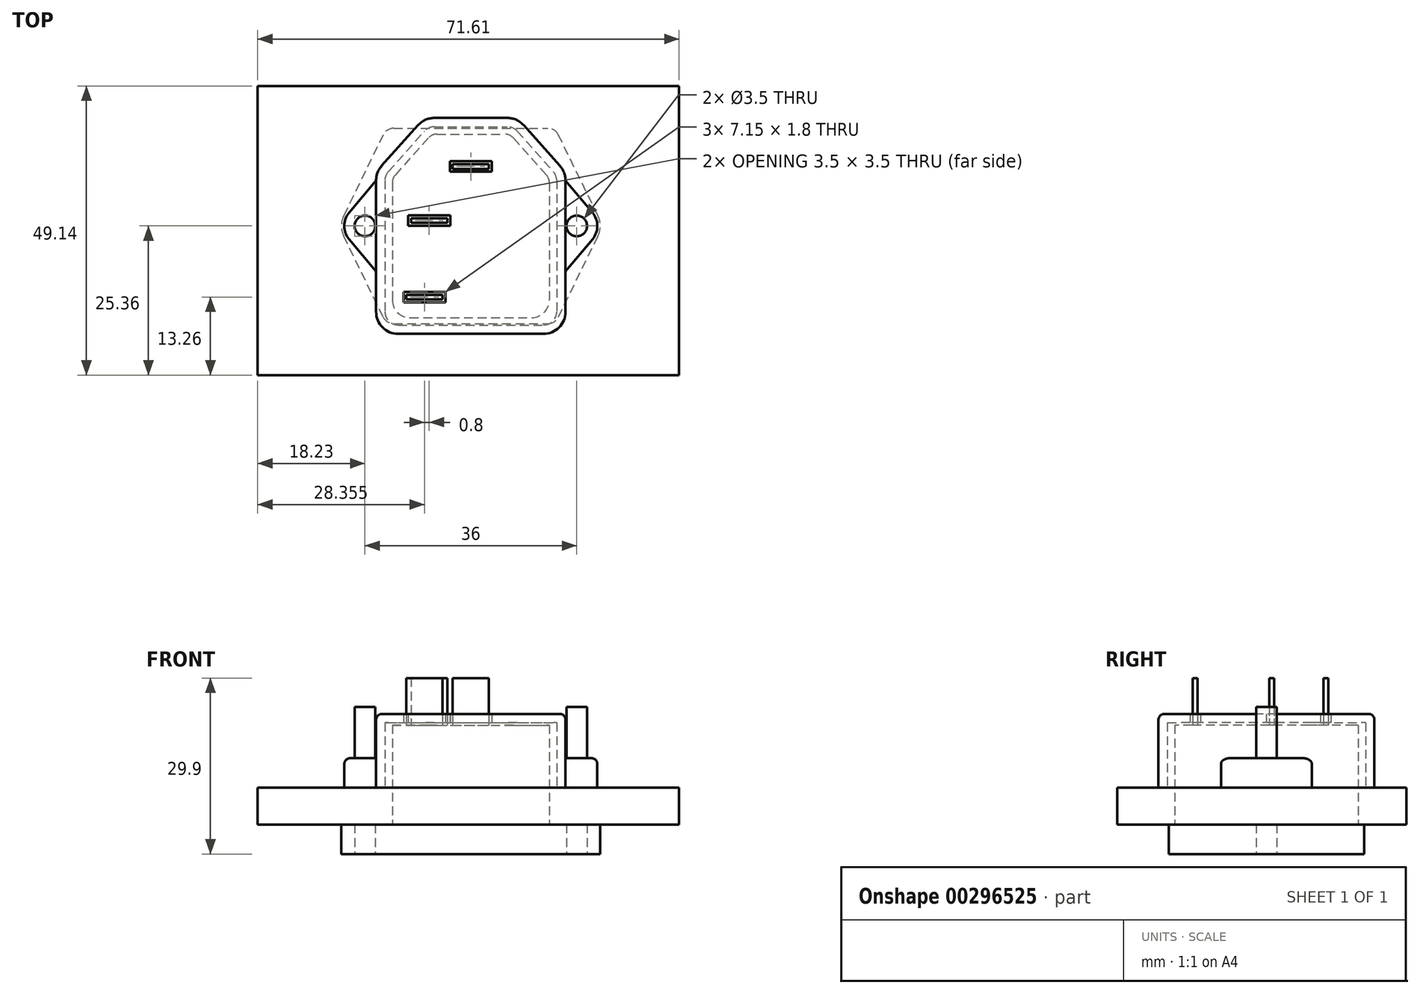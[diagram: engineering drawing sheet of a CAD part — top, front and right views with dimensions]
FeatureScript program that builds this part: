
annotation { "Feature Type Name" : "Feature", "Feature Type Description" : "" }
export const myFeature = defineFeature(function(context is Context, id is Id, definition is map)
    precondition{}
    {
        {
            var Q0;
            Q0=qCreatedBy(makeId("Top.planeOp"),FACE);
            var sketch = newSketch(context, id + "F0", { "sketchPlane" : qUnion([Q0])});
            skLineSegment(sketch, "E0.bottom", {"start": v(-5.75, 13.24) * mm, "end": v(5.75, 13.24) * mm});
            skLineSegment(sketch, "E0.top", {"start": v(-10.35, -17.96) * mm, "end": v(10.35, -17.96) * mm});
            skLineSegment(sketch, "E0.left", {"start": v(-13.35, 4.98) * mm, "end": v(-13.35, -14.96) * mm});
            skLineSegment(sketch, "E0.right", {"start": v(13.35, 4.98) * mm, "end": v(13.35, -14.96) * mm});
            skLineSegment(sketch, "E1", {"start": v(-7.25, 12.57) * mm, "end": v(-12.84, 6.3) * mm});
            skLineSegment(sketch, "E2", {"start": v(7.25, 12.57) * mm, "end": v(12.84, 6.3) * mm});
            skPoint(sketch, "E3.orphan", {"position": v(-13.35, 13.24) * mm});
            skPoint(sketch, "E4.orphan", {"position": v(13.35, 13.24) * mm});
            skPoint(sketch, "E5.visualSharp", {"position": v(-6.65, 13.24) * mm});
            skArc(sketch, "E5.filletArc", {"start": v(-5.75, 13.24) * mm, "mid": v(-6.57, 13.07) * mm, "end": v(-7.25, 12.57) * mm});
            skPoint(sketch, "E6.visualSharp", {"position": v(6.65, 13.24) * mm});
            skArc(sketch, "E6.filletArc", {"start": v(7.25, 12.57) * mm, "mid": v(6.57, 13.07) * mm, "end": v(5.75, 13.24) * mm});
            skPoint(sketch, "E7.visualSharp", {"position": v(13.35, 5.74) * mm});
            skArc(sketch, "E7.filletArc", {"start": v(13.35, 4.98) * mm, "mid": v(13.22, 5.69) * mm, "end": v(12.84, 6.3) * mm});
            skPoint(sketch, "E8.visualSharp", {"position": v(-13.35, 5.74) * mm});
            skArc(sketch, "E8.filletArc", {"start": v(-12.84, 6.3) * mm, "mid": v(-13.22, 5.69) * mm, "end": v(-13.35, 4.98) * mm});
            skPoint(sketch, "E9.visualSharp", {"position": v(-13.35, -17.96) * mm});
            skArc(sketch, "E9.filletArc", {"start": v(-13.35, -14.96) * mm, "mid": v(-12.47, -17.08) * mm, "end": v(-10.35, -17.96) * mm});
            skPoint(sketch, "E10.visualSharp", {"position": v(13.35, -17.96) * mm});
            skArc(sketch, "E10.filletArc", {"start": v(10.35, -17.96) * mm, "mid": v(12.47, -17.08) * mm, "end": v(13.35, -14.96) * mm});
            skSolve(sketch);
        }
        {
            var Q0;
            Q0=makeQuery(id+"F0.imprint","IMPRINT",FACE,{"disambiguationData":[TD([[makeQuery(id+"F0.imprint","IMPRINT",EDGE,{"derivedFrom":sQuery(id+"F0.wireOp",EDGE,"E0.bottom")}),-1.0]])]});
            extrude(context, id + "F1", {"entities" : qUnion([Q0]), "depth" : 16.9 * mm});
        }
        {
            var Q0;
            Q0=makeQuery(id+"F1.opExtrude","CAP_FACE",FACE,{"disambiguationData":[OSD([sQuery(id+"F0.wireOp",EDGE,"E0.bottom"),sQuery(id+"F0.wireOp",EDGE,"E0.top"),sQuery(id+"F0.wireOp",EDGE,"E0.left"),sQuery(id+"F0.wireOp",EDGE,"E0.right"),sQuery(id+"F0.wireOp",EDGE,"E1"),sQuery(id+"F0.wireOp",EDGE,"E2"),sQuery(id+"F0.wireOp",EDGE,"E5.filletArc"),sQuery(id+"F0.wireOp",EDGE,"E6.filletArc"),sQuery(id+"F0.wireOp",EDGE,"E7.filletArc"),sQuery(id+"F0.wireOp",EDGE,"E8.filletArc"),sQuery(id+"F0.wireOp",EDGE,"E9.filletArc"),sQuery(id+"F0.wireOp",EDGE,"E10.filletArc")])],"isStart":false});
            var sketch = newSketch(context, id + "F2", { "sketchPlane" : qUnion([Q0])});
            skLineSegment(sketch, "E11.bottom", {"start": v(-3.08, 8.14) * mm, "end": v(3.08, 8.14) * mm});
            skLineSegment(sketch, "E11.top", {"start": v(-3.08, 7.34) * mm, "end": v(3.07, 7.34) * mm});
            skLineSegment(sketch, "E11.left", {"start": v(-3.08, 8.14) * mm, "end": v(-3.08, 7.34) * mm});
            skLineSegment(sketch, "E11.right", {"start": v(3.08, 8.14) * mm, "end": v(3.08, 7.34) * mm});
            skLineSegment(sketch, "E12.bottom", {"start": v(-10.15, -1.06) * mm, "end": v(-4, -1.06) * mm});
            skLineSegment(sketch, "E12.top", {"start": v(-10.15, -1.86) * mm, "end": v(-4, -1.86) * mm});
            skLineSegment(sketch, "E12.left", {"start": v(-10.15, -1.06) * mm, "end": v(-10.15, -1.86) * mm});
            skLineSegment(sketch, "E12.right", {"start": v(-4, -1.06) * mm, "end": v(-4, -1.86) * mm});
            skLineSegment(sketch, "E13.bottom", {"start": v(-10.95, -14.06) * mm, "end": v(-4.8, -14.06) * mm});
            skLineSegment(sketch, "E13.top", {"start": v(-10.95, -14.86) * mm, "end": v(-4.8, -14.86) * mm});
            skLineSegment(sketch, "E13.left", {"start": v(-10.95, -14.06) * mm, "end": v(-10.95, -14.86) * mm});
            skLineSegment(sketch, "E13.right", {"start": v(-4.8, -14.06) * mm, "end": v(-4.8, -14.86) * mm});
            skSolve(sketch);
        }
        {
            var Q0;
            Q0 = qSketchRegion(id + "F2", true);
            extrude(context, id + "F3", {"entities" : qUnion([Q0]), "operationType" : NewBodyOperationType.ADD, "depth" : 8 * mm});
        }
        {
            var Q0;
            Q0=makeQuery(id+"F1.opExtrude","CAP_FACE",FACE,{"disambiguationData":[OSD([sQuery(id+"F0.wireOp",EDGE,"E0.bottom"),sQuery(id+"F0.wireOp",EDGE,"E0.top"),sQuery(id+"F0.wireOp",EDGE,"E0.left"),sQuery(id+"F0.wireOp",EDGE,"E0.right"),sQuery(id+"F0.wireOp",EDGE,"E1"),sQuery(id+"F0.wireOp",EDGE,"E2"),sQuery(id+"F0.wireOp",EDGE,"E5.filletArc"),sQuery(id+"F0.wireOp",EDGE,"E6.filletArc"),sQuery(id+"F0.wireOp",EDGE,"E7.filletArc"),sQuery(id+"F0.wireOp",EDGE,"E8.filletArc"),sQuery(id+"F0.wireOp",EDGE,"E9.filletArc"),sQuery(id+"F0.wireOp",EDGE,"E10.filletArc")])],"isStart":true});
            var sketch = newSketch(context, id + "F4", { "sketchPlane" : qUnion([Q0])});
            skLineSegment(sketch, "E14.bottom", {"start": v(-13.1, 18.96) * mm, "end": v(13.1, 18.96) * mm});
            skLineSegment(sketch, "E14.top", {"start": v(-13.1, -14.24) * mm, "end": v(13.1, -14.24) * mm});
            skLineSegment(sketch, "E14.left", {"start": v(-14.35, 18.96) * mm, "end": v(-14.35, 18.52) * mm});
            skLineSegment(sketch, "E14.right", {"start": v(14.35, 18.96) * mm, "end": v(14.35, 18.52) * mm});
            skLineSegment(sketch, "E15", {"start": v(-20.93, 2.36) * mm, "end": v(38.8, 2.36) * mm, "construction": true});
            skCircle(sketch, "E16", {"center": v(18, 2.36) * mm, "radius": 1.75 * mm});
            skCircle(sketch, "E17", {"center": v(-18, 2.36) * mm, "radius": 1.75 * mm});
            skArc(sketch, "E18", {"start": v(-21.6, 4.11) * mm, "mid": v(-22, 2.36) * mm, "end": v(-21.6, 0.6) * mm});
            skArc(sketch, "E19", {"start": v(21.6, 0.6) * mm, "mid": v(22, 2.36) * mm, "end": v(21.6, 4.11) * mm});
            skLineSegment(sketch, "E20", {"start": v(-14.9, 17.84) * mm, "end": v(-21.6, 4.11) * mm});
            skLineSegment(sketch, "E21", {"start": v(-14.9, -13.12) * mm, "end": v(-21.6, 0.6) * mm});
            skLineSegment(sketch, "E22", {"start": v(14.9, 17.84) * mm, "end": v(21.6, 4.11) * mm});
            skLineSegment(sketch, "E23", {"start": v(21.6, 0.6) * mm, "end": v(14.9, -13.12) * mm});
            skPoint(sketch, "E24.visualSharp", {"position": v(-14.35, 18.96) * mm});
            skArc(sketch, "E24.filletArc", {"start": v(-13.1, 18.96) * mm, "mid": v(-14.16, 18.66) * mm, "end": v(-14.9, 17.84) * mm});
            skPoint(sketch, "E25.visualSharp", {"position": v(14.35, 18.96) * mm});
            skArc(sketch, "E25.filletArc", {"start": v(14.9, 17.84) * mm, "mid": v(14.16, 18.66) * mm, "end": v(13.1, 18.96) * mm});
            skPoint(sketch, "E26.visualSharp", {"position": v(-14.35, -14.24) * mm});
            skArc(sketch, "E26.filletArc", {"start": v(-14.9, -13.12) * mm, "mid": v(-14.16, -13.94) * mm, "end": v(-13.1, -14.24) * mm});
            skPoint(sketch, "E27.visualSharp", {"position": v(14.35, -14.24) * mm});
            skArc(sketch, "E27.filletArc", {"start": v(13.1, -14.24) * mm, "mid": v(14.16, -13.94) * mm, "end": v(14.9, -13.12) * mm});
            skLineSegment(sketch, "E28.trimOffspring", {"start": v(-14.35, -13.8) * mm, "end": v(-14.35, -14.24) * mm});
            skLineSegment(sketch, "E29.trimOffspring", {"start": v(14.35, -13.8) * mm, "end": v(14.35, -14.24) * mm});
            skSolve(sketch);
        }
        {
            var Q0;
            Q0 = qSketchRegion(id + "F4", true);
            extrude(context, id + "F5", {"entities" : qUnion([Q0]), "operationType" : NewBodyOperationType.ADD, "depth" : 5 * mm});
        }
        {
            var Q0;
            Q0=makeQuery(id+"F5.opExtrude","CAP_FACE",FACE,{"disambiguationData":[OSD([sQuery(id+"F4.wireOp",EDGE,"E14.bottom"),sQuery(id+"F4.wireOp",EDGE,"E14.top"),sQuery(id+"F4.wireOp",EDGE,"E16"),sQuery(id+"F4.wireOp",EDGE,"E17"),sQuery(id+"F4.wireOp",EDGE,"E18"),sQuery(id+"F4.wireOp",EDGE,"E19"),sQuery(id+"F4.wireOp",EDGE,"E20"),sQuery(id+"F4.wireOp",EDGE,"E21"),sQuery(id+"F4.wireOp",EDGE,"E22"),sQuery(id+"F4.wireOp",EDGE,"E23"),sQuery(id+"F4.wireOp",EDGE,"E24.filletArc"),sQuery(id+"F4.wireOp",EDGE,"E25.filletArc"),sQuery(id+"F4.wireOp",EDGE,"E26.filletArc"),sQuery(id+"F4.wireOp",EDGE,"E27.filletArc")])],"isStart":true});
            var sketch = newSketch(context, id + "F6", { "sketchPlane" : qUnion([Q0])});
            skLineSegment(sketch, "E30.bottom", {"start": v(-36.23, 21.42) * mm, "end": v(35.38, 21.42) * mm});
            skLineSegment(sketch, "E30.top", {"start": v(-36.23, -27.72) * mm, "end": v(35.38, -27.72) * mm});
            skLineSegment(sketch, "E30.left", {"start": v(-36.23, 21.42) * mm, "end": v(-36.23, -27.72) * mm});
            skLineSegment(sketch, "E30.right", {"start": v(35.38, 21.42) * mm, "end": v(35.38, -27.72) * mm});
            skSolve(sketch);
        }
        {
            var Q0;
            Q0 = qSketchRegion(id + "F6", true);
            extrude(context, id + "F7", {"entities" : qUnion([Q0]), "depth" : 6.3 * mm});
        }
        {
            var Q0;
            Q0=makeQuery(id+"F7.opExtrude","CAP_FACE",FACE,{"disambiguationData":[OSD([sQuery(id+"F6.wireOp",EDGE,"E30.bottom"),sQuery(id+"F6.wireOp",EDGE,"E30.top"),sQuery(id+"F6.wireOp",EDGE,"E30.left"),sQuery(id+"F6.wireOp",EDGE,"E30.right")])],"isStart":false});
            var sketch = newSketch(context, id + "F8", { "sketchPlane" : qUnion([Q0])});
            skLineSegment(sketch, "E31.bottom", {"start": v(-6.2, 15.24) * mm, "end": v(6.2, 15.24) * mm});
            skLineSegment(sketch, "E31.top", {"start": v(-12.35, -19.96) * mm, "end": v(12.35, -19.96) * mm});
            skLineSegment(sketch, "E31.left", {"start": v(-15.35, 5.36) * mm, "end": v(-15.35, -16.96) * mm});
            skLineSegment(sketch, "E31.right", {"start": v(15.35, 5.36) * mm, "end": v(15.35, -16.96) * mm});
            skLineSegment(sketch, "E32", {"start": v(-14.59, 7.36) * mm, "end": v(-8.44, 14.24) * mm});
            skLineSegment(sketch, "E33", {"start": v(8.44, 14.24) * mm, "end": v(14.59, 7.36) * mm});
            skPoint(sketch, "E34.visualSharp", {"position": v(-15.35, -19.96) * mm});
            skArc(sketch, "E34.filletArc", {"start": v(-15.35, -16.96) * mm, "mid": v(-14.47, -19.08) * mm, "end": v(-12.35, -19.96) * mm});
            skPoint(sketch, "E35.visualSharp", {"position": v(15.35, -19.96) * mm});
            skArc(sketch, "E35.filletArc", {"start": v(12.35, -19.96) * mm, "mid": v(14.47, -19.08) * mm, "end": v(15.35, -16.96) * mm});
            skPoint(sketch, "E36.visualSharp", {"position": v(15.35, 6.5) * mm});
            skArc(sketch, "E36.filletArc", {"start": v(15.35, 5.36) * mm, "mid": v(15.15, 6.43) * mm, "end": v(14.59, 7.36) * mm});
            skPoint(sketch, "E37.visualSharp", {"position": v(7.55, 15.24) * mm});
            skArc(sketch, "E37.filletArc", {"start": v(8.44, 14.24) * mm, "mid": v(7.43, 14.98) * mm, "end": v(6.2, 15.24) * mm});
            skPoint(sketch, "E38.visualSharp", {"position": v(-7.55, 15.24) * mm});
            skArc(sketch, "E38.filletArc", {"start": v(-6.2, 15.24) * mm, "mid": v(-7.43, 14.98) * mm, "end": v(-8.44, 14.24) * mm});
            skPoint(sketch, "E39.visualSharp", {"position": v(-15.35, 6.5) * mm});
            skArc(sketch, "E39.filletArc", {"start": v(-14.59, 7.36) * mm, "mid": v(-15.15, 6.43) * mm, "end": v(-15.35, 5.36) * mm});
            skArc(sketch, "E40.0.startCap", {"start": v(-14.03, 6.86) * mm, "mid": v(-15.09, 6.8) * mm, "end": v(-15.15, 7.86) * mm});
            skArc(sketch, "E40.0.endCap", {"start": v(-9, 14.74) * mm, "mid": v(-7.94, 14.8) * mm, "end": v(-7.88, 13.74) * mm});
            skLineSegment(sketch, "E40.0.left", {"start": v(-15.15, 7.86) * mm, "end": v(-9, 14.74) * mm});
            skLineSegment(sketch, "E40.0.right", {"start": v(-14.03, 6.86) * mm, "end": v(-7.88, 13.74) * mm});
            skArc(sketch, "E40.1.startCap", {"start": v(-6.2, 15.99) * mm, "mid": v(-5.45, 15.24) * mm, "end": v(-6.2, 14.49) * mm});
            skArc(sketch, "E40.1.endCap", {"start": v(-7.88, 13.74) * mm, "mid": v(-8.94, 13.68) * mm, "end": v(-9, 14.74) * mm});
            skArc(sketch, "E40.1.left", {"start": v(-6.2, 14.49) * mm, "mid": v(-7.12, 14.3) * mm, "end": v(-7.88, 13.74) * mm});
            skArc(sketch, "E40.1.right", {"start": v(-6.2, 15.99) * mm, "mid": v(-7.73, 15.66) * mm, "end": v(-9, 14.74) * mm});
            skArc(sketch, "E40.2.startCap", {"start": v(-6.2, 14.49) * mm, "mid": v(-6.95, 15.24) * mm, "end": v(-6.2, 15.99) * mm});
            skArc(sketch, "E40.2.endCap", {"start": v(6.2, 15.99) * mm, "mid": v(6.95, 15.24) * mm, "end": v(6.2, 14.49) * mm});
            skLineSegment(sketch, "E40.2.left", {"start": v(-6.2, 15.99) * mm, "end": v(6.2, 15.99) * mm});
            skLineSegment(sketch, "E40.2.right", {"start": v(-6.2, 14.49) * mm, "end": v(6.2, 14.49) * mm});
            skArc(sketch, "E40.3.startCap", {"start": v(9, 14.74) * mm, "mid": v(8.94, 13.68) * mm, "end": v(7.88, 13.74) * mm});
            skArc(sketch, "E40.3.endCap", {"start": v(6.2, 14.49) * mm, "mid": v(5.45, 15.24) * mm, "end": v(6.2, 15.99) * mm});
            skArc(sketch, "E40.3.left", {"start": v(7.88, 13.74) * mm, "mid": v(7.12, 14.3) * mm, "end": v(6.2, 14.49) * mm});
            skArc(sketch, "E40.3.right", {"start": v(9, 14.74) * mm, "mid": v(7.73, 15.66) * mm, "end": v(6.2, 15.99) * mm});
            skArc(sketch, "E40.4.startCap", {"start": v(7.88, 13.74) * mm, "mid": v(7.94, 14.8) * mm, "end": v(9, 14.74) * mm});
            skArc(sketch, "E40.4.endCap", {"start": v(15.15, 7.86) * mm, "mid": v(15.09, 6.8) * mm, "end": v(14.03, 6.86) * mm});
            skLineSegment(sketch, "E40.4.left", {"start": v(9, 14.74) * mm, "end": v(15.15, 7.86) * mm});
            skLineSegment(sketch, "E40.4.right", {"start": v(7.88, 13.74) * mm, "end": v(14.03, 6.86) * mm});
            skArc(sketch, "E40.5.startCap", {"start": v(16.1, 5.36) * mm, "mid": v(15.35, 4.6) * mm, "end": v(14.6, 5.36) * mm});
            skArc(sketch, "E40.5.endCap", {"start": v(14.03, 6.86) * mm, "mid": v(14.09, 7.92) * mm, "end": v(15.15, 7.86) * mm});
            skArc(sketch, "E40.5.left", {"start": v(14.6, 5.36) * mm, "mid": v(14.45, 6.16) * mm, "end": v(14.03, 6.86) * mm});
            skArc(sketch, "E40.5.right", {"start": v(16.1, 5.36) * mm, "mid": v(15.85, 6.7) * mm, "end": v(15.15, 7.86) * mm});
            skArc(sketch, "E40.6.startCap", {"start": v(14.6, 5.36) * mm, "mid": v(15.35, 6.1) * mm, "end": v(16.1, 5.36) * mm});
            skArc(sketch, "E40.6.endCap", {"start": v(16.1, -16.96) * mm, "mid": v(15.35, -17.71) * mm, "end": v(14.6, -16.96) * mm});
            skLineSegment(sketch, "E40.6.left", {"start": v(16.1, 5.36) * mm, "end": v(16.1, -16.96) * mm});
            skLineSegment(sketch, "E40.6.right", {"start": v(14.6, 5.36) * mm, "end": v(14.6, -16.96) * mm});
            skArc(sketch, "E40.7.startCap", {"start": v(12.35, -20.71) * mm, "mid": v(11.6, -19.96) * mm, "end": v(12.35, -19.21) * mm});
            skArc(sketch, "E40.7.endCap", {"start": v(14.6, -16.96) * mm, "mid": v(15.35, -16.21) * mm, "end": v(16.1, -16.96) * mm});
            skArc(sketch, "E40.7.left", {"start": v(12.35, -19.21) * mm, "mid": v(13.94, -18.55) * mm, "end": v(14.6, -16.96) * mm});
            skArc(sketch, "E40.7.right", {"start": v(12.35, -20.71) * mm, "mid": v(15, -19.61) * mm, "end": v(16.1, -16.96) * mm});
            skArc(sketch, "E40.8.startCap", {"start": v(-12.35, -20.71) * mm, "mid": v(-13.1, -19.96) * mm, "end": v(-12.35, -19.21) * mm});
            skArc(sketch, "E40.8.endCap", {"start": v(12.35, -19.21) * mm, "mid": v(13.1, -19.96) * mm, "end": v(12.35, -20.71) * mm});
            skLineSegment(sketch, "E40.8.left", {"start": v(-12.35, -19.21) * mm, "end": v(12.35, -19.21) * mm});
            skLineSegment(sketch, "E40.8.right", {"start": v(-12.35, -20.71) * mm, "end": v(12.35, -20.71) * mm});
            skArc(sketch, "E40.9.startCap", {"start": v(-16.1, -16.96) * mm, "mid": v(-15.35, -16.21) * mm, "end": v(-14.6, -16.96) * mm});
            skArc(sketch, "E40.9.endCap", {"start": v(-12.35, -19.21) * mm, "mid": v(-11.6, -19.96) * mm, "end": v(-12.35, -20.71) * mm});
            skArc(sketch, "E40.9.left", {"start": v(-14.6, -16.96) * mm, "mid": v(-13.94, -18.55) * mm, "end": v(-12.35, -19.21) * mm});
            skArc(sketch, "E40.9.right", {"start": v(-16.1, -16.96) * mm, "mid": v(-15, -19.61) * mm, "end": v(-12.35, -20.71) * mm});
            skArc(sketch, "E40.10.startCap", {"start": v(-16.1, 5.36) * mm, "mid": v(-15.35, 6.1) * mm, "end": v(-14.6, 5.36) * mm});
            skArc(sketch, "E40.10.endCap", {"start": v(-14.6, -16.96) * mm, "mid": v(-15.35, -17.71) * mm, "end": v(-16.1, -16.96) * mm});
            skLineSegment(sketch, "E40.10.left", {"start": v(-14.6, 5.36) * mm, "end": v(-14.6, -16.96) * mm});
            skLineSegment(sketch, "E40.10.right", {"start": v(-16.1, 5.36) * mm, "end": v(-16.1, -16.96) * mm});
            skArc(sketch, "E40.11.startCap", {"start": v(-15.15, 7.86) * mm, "mid": v(-14.09, 7.92) * mm, "end": v(-14.03, 6.86) * mm});
            skArc(sketch, "E40.11.endCap", {"start": v(-14.6, 5.36) * mm, "mid": v(-15.35, 4.6) * mm, "end": v(-16.1, 5.36) * mm});
            skArc(sketch, "E40.11.left", {"start": v(-14.03, 6.86) * mm, "mid": v(-14.45, 6.16) * mm, "end": v(-14.6, 5.36) * mm});
            skArc(sketch, "E40.11.right", {"start": v(-15.15, 7.86) * mm, "mid": v(-15.85, 6.7) * mm, "end": v(-16.1, 5.36) * mm});
            skSolve(sketch);
        }
        {
            var Q0;
            {var subQ5=sQuery(id+"F8.wireOp",EDGE,"E40.0.right");Q0=makeQuery(id+"F8.imprint","IMPRINT",FACE,{"disambiguationData":[TD([[makeQuery(id+"F8.imprint","IMPRINT",EDGE,{"derivedFrom":subQ5}),1.0]])]});}
            var Q1;
            {var subQ0=sQuery(id+"F8.wireOp",EDGE,"E38.filletArc");var subQ1=sQuery(id+"F8.wireOp",EDGE,"E32");var subQ2=makeQuery(id+"F8.imprint","INTERSECT",VERTEX,{"derivedFrom":[subQ1,subQ0]});Q1=makeQuery(id+"F8.imprint","IMPRINT",FACE,{"disambiguationData":[TD([[makeQuery(id+"F8.imprint","IMPRINT",EDGE,{"disambiguationData":[TD([[subQ2,1.0]])],"derivedFrom":subQ1}),-1.0]])]});}
            var Q2;
            {var subQ5=sQuery(id+"F8.wireOp",EDGE,"E40.1.left");Q2=makeQuery(id+"F8.imprint","IMPRINT",FACE,{"disambiguationData":[TD([[makeQuery(id+"F8.imprint","IMPRINT",EDGE,{"derivedFrom":subQ5}),-1.0]])]});}
            var Q3;
            {var subQ0=sQuery(id+"F8.wireOp",EDGE,"E38.filletArc");var subQ1=sQuery(id+"F8.wireOp",EDGE,"E31.bottom");var subQ2=makeQuery(id+"F8.imprint","INTERSECT",VERTEX,{"derivedFrom":[subQ1,subQ0]});Q3=makeQuery(id+"F8.imprint","IMPRINT",FACE,{"disambiguationData":[TD([[makeQuery(id+"F8.imprint","IMPRINT",EDGE,{"disambiguationData":[TD([[subQ2,-1.0]])],"derivedFrom":subQ1}),-1.0]])]});}
            var Q4;
            {var subQ5=sQuery(id+"F8.wireOp",EDGE,"E40.2.right");Q4=makeQuery(id+"F8.imprint","IMPRINT",FACE,{"disambiguationData":[TD([[makeQuery(id+"F8.imprint","IMPRINT",EDGE,{"derivedFrom":subQ5}),1.0]])]});}
            var Q5;
            {var subQ0=sQuery(id+"F8.wireOp",EDGE,"E37.filletArc");var subQ1=sQuery(id+"F8.wireOp",EDGE,"E31.bottom");var subQ2=makeQuery(id+"F8.imprint","INTERSECT",VERTEX,{"derivedFrom":[subQ1,subQ0]});Q5=makeQuery(id+"F8.imprint","IMPRINT",FACE,{"disambiguationData":[TD([[makeQuery(id+"F8.imprint","IMPRINT",EDGE,{"disambiguationData":[TD([[subQ2,1.0]])],"derivedFrom":subQ1}),-1.0]])]});}
            var Q6;
            {var subQ5=sQuery(id+"F8.wireOp",EDGE,"E40.3.left");Q6=makeQuery(id+"F8.imprint","IMPRINT",FACE,{"disambiguationData":[TD([[makeQuery(id+"F8.imprint","IMPRINT",EDGE,{"derivedFrom":subQ5}),-1.0]])]});}
            var Q7;
            {var subQ0=sQuery(id+"F8.wireOp",EDGE,"E37.filletArc");var subQ1=sQuery(id+"F8.wireOp",EDGE,"E33");var subQ2=makeQuery(id+"F8.imprint","INTERSECT",VERTEX,{"derivedFrom":[subQ1,subQ0]});Q7=makeQuery(id+"F8.imprint","IMPRINT",FACE,{"disambiguationData":[TD([[makeQuery(id+"F8.imprint","IMPRINT",EDGE,{"disambiguationData":[TD([[subQ2,-1.0]])],"derivedFrom":subQ1}),-1.0]])]});}
            var Q8;
            {var subQ5=sQuery(id+"F8.wireOp",EDGE,"E40.4.right");Q8=makeQuery(id+"F8.imprint","IMPRINT",FACE,{"disambiguationData":[TD([[makeQuery(id+"F8.imprint","IMPRINT",EDGE,{"derivedFrom":subQ5}),1.0]])]});}
            var Q9;
            {var subQ0=sQuery(id+"F8.wireOp",EDGE,"E36.filletArc");var subQ1=sQuery(id+"F8.wireOp",EDGE,"E33");var subQ2=makeQuery(id+"F8.imprint","INTERSECT",VERTEX,{"derivedFrom":[subQ1,subQ0]});Q9=makeQuery(id+"F8.imprint","IMPRINT",FACE,{"disambiguationData":[TD([[makeQuery(id+"F8.imprint","IMPRINT",EDGE,{"disambiguationData":[TD([[subQ2,1.0]])],"derivedFrom":subQ1}),-1.0]])]});}
            var Q10;
            {var subQ5=sQuery(id+"F8.wireOp",EDGE,"E40.5.left");Q10=makeQuery(id+"F8.imprint","IMPRINT",FACE,{"disambiguationData":[TD([[makeQuery(id+"F8.imprint","IMPRINT",EDGE,{"derivedFrom":subQ5}),-1.0]])]});}
            var Q11;
            {var subQ0=sQuery(id+"F8.wireOp",EDGE,"E36.filletArc");var subQ1=sQuery(id+"F8.wireOp",EDGE,"E31.right");var subQ2=makeQuery(id+"F8.imprint","INTERSECT",VERTEX,{"derivedFrom":[subQ1,subQ0]});Q11=makeQuery(id+"F8.imprint","IMPRINT",FACE,{"disambiguationData":[TD([[makeQuery(id+"F8.imprint","IMPRINT",EDGE,{"disambiguationData":[TD([[subQ2,-1.0]])],"derivedFrom":subQ1}),-1.0]])]});}
            var Q12;
            {var subQ5=sQuery(id+"F8.wireOp",EDGE,"E40.6.right");Q12=makeQuery(id+"F8.imprint","IMPRINT",FACE,{"disambiguationData":[TD([[makeQuery(id+"F8.imprint","IMPRINT",EDGE,{"derivedFrom":subQ5}),1.0]])]});}
            var Q13;
            {var subQ0=sQuery(id+"F8.wireOp",EDGE,"E35.filletArc");var subQ1=sQuery(id+"F8.wireOp",EDGE,"E31.right");var subQ2=makeQuery(id+"F8.imprint","INTERSECT",VERTEX,{"derivedFrom":[subQ1,subQ0]});Q13=makeQuery(id+"F8.imprint","IMPRINT",FACE,{"disambiguationData":[TD([[makeQuery(id+"F8.imprint","IMPRINT",EDGE,{"disambiguationData":[TD([[subQ2,1.0]])],"derivedFrom":subQ1}),-1.0]])]});}
            var Q14;
            {var subQ5=sQuery(id+"F8.wireOp",EDGE,"E40.7.left");Q14=makeQuery(id+"F8.imprint","IMPRINT",FACE,{"disambiguationData":[TD([[makeQuery(id+"F8.imprint","IMPRINT",EDGE,{"derivedFrom":subQ5}),-1.0]])]});}
            var Q15;
            {var subQ0=sQuery(id+"F8.wireOp",EDGE,"E35.filletArc");var subQ1=sQuery(id+"F8.wireOp",EDGE,"E31.top");var subQ2=makeQuery(id+"F8.imprint","INTERSECT",VERTEX,{"derivedFrom":[subQ1,subQ0]});Q15=makeQuery(id+"F8.imprint","IMPRINT",FACE,{"disambiguationData":[TD([[makeQuery(id+"F8.imprint","IMPRINT",EDGE,{"disambiguationData":[TD([[subQ2,1.0]])],"derivedFrom":subQ1}),1.0]])]});}
            var Q16;
            {var subQ5=sQuery(id+"F8.wireOp",EDGE,"E40.8.left");Q16=makeQuery(id+"F8.imprint","IMPRINT",FACE,{"disambiguationData":[TD([[makeQuery(id+"F8.imprint","IMPRINT",EDGE,{"derivedFrom":subQ5}),-1.0]])]});}
            var Q17;
            {var subQ5=sQuery(id+"F8.wireOp",EDGE,"E40.9.left");Q17=makeQuery(id+"F8.imprint","IMPRINT",FACE,{"disambiguationData":[TD([[makeQuery(id+"F8.imprint","IMPRINT",EDGE,{"derivedFrom":subQ5}),-1.0]])]});}
            var Q18;
            {var subQ0=sQuery(id+"F8.wireOp",EDGE,"E34.filletArc");var subQ1=sQuery(id+"F8.wireOp",EDGE,"E31.left");var subQ2=makeQuery(id+"F8.imprint","INTERSECT",VERTEX,{"derivedFrom":[subQ1,subQ0]});Q18=makeQuery(id+"F8.imprint","IMPRINT",FACE,{"disambiguationData":[TD([[makeQuery(id+"F8.imprint","IMPRINT",EDGE,{"disambiguationData":[TD([[subQ2,1.0]])],"derivedFrom":subQ1}),1.0]])]});}
            var Q19;
            {var subQ5=sQuery(id+"F8.wireOp",EDGE,"E40.10.left");Q19=makeQuery(id+"F8.imprint","IMPRINT",FACE,{"disambiguationData":[TD([[makeQuery(id+"F8.imprint","IMPRINT",EDGE,{"derivedFrom":subQ5}),-1.0]])]});}
            var Q20;
            {var subQ0=sQuery(id+"F8.wireOp",EDGE,"E39.filletArc");var subQ1=sQuery(id+"F8.wireOp",EDGE,"E31.left");var subQ2=makeQuery(id+"F8.imprint","INTERSECT",VERTEX,{"derivedFrom":[subQ1,subQ0]});Q20=makeQuery(id+"F8.imprint","IMPRINT",FACE,{"disambiguationData":[TD([[makeQuery(id+"F8.imprint","IMPRINT",EDGE,{"disambiguationData":[TD([[subQ2,-1.0]])],"derivedFrom":subQ1}),1.0]])]});}
            var Q21;
            {var subQ0=sQuery(id+"F8.wireOp",EDGE,"E39.filletArc");var subQ1=sQuery(id+"F8.wireOp",EDGE,"E32");var subQ2=makeQuery(id+"F8.imprint","INTERSECT",VERTEX,{"derivedFrom":[subQ1,subQ0]});Q21=makeQuery(id+"F8.imprint","IMPRINT",FACE,{"disambiguationData":[TD([[makeQuery(id+"F8.imprint","IMPRINT",EDGE,{"disambiguationData":[TD([[subQ2,-1.0]])],"derivedFrom":subQ1}),-1.0]])]});}
            var Q22;
            {var subQ5=sQuery(id+"F8.wireOp",EDGE,"E40.11.left");Q22=makeQuery(id+"F8.imprint","IMPRINT",FACE,{"disambiguationData":[TD([[makeQuery(id+"F8.imprint","IMPRINT",EDGE,{"derivedFrom":subQ5}),-1.0]])]});}
            var Q23;
            {var subQ5=sQuery(id+"F8.wireOp",EDGE,"E40.0.left");Q23=makeQuery(id+"F8.imprint","IMPRINT",FACE,{"disambiguationData":[TD([[makeQuery(id+"F8.imprint","IMPRINT",EDGE,{"derivedFrom":subQ5}),-1.0]])]});}
            var Q24;
            {var subQ0=sQuery(id+"F8.wireOp",EDGE,"E39.filletArc");var subQ1=sQuery(id+"F8.wireOp",EDGE,"E32");var subQ2=makeQuery(id+"F8.imprint","INTERSECT",VERTEX,{"derivedFrom":[subQ1,subQ0]});Q24=makeQuery(id+"F8.imprint","IMPRINT",FACE,{"disambiguationData":[TD([[makeQuery(id+"F8.imprint","IMPRINT",EDGE,{"disambiguationData":[TD([[subQ2,-1.0]])],"derivedFrom":subQ1}),1.0]])]});}
            var Q25;
            {var subQ5=sQuery(id+"F8.wireOp",EDGE,"E40.11.right");Q25=makeQuery(id+"F8.imprint","IMPRINT",FACE,{"disambiguationData":[TD([[makeQuery(id+"F8.imprint","IMPRINT",EDGE,{"derivedFrom":subQ5}),1.0]])]});}
            var Q26;
            {var subQ0=sQuery(id+"F8.wireOp",EDGE,"E39.filletArc");var subQ1=sQuery(id+"F8.wireOp",EDGE,"E31.left");var subQ2=makeQuery(id+"F8.imprint","INTERSECT",VERTEX,{"derivedFrom":[subQ1,subQ0]});Q26=makeQuery(id+"F8.imprint","IMPRINT",FACE,{"disambiguationData":[TD([[makeQuery(id+"F8.imprint","IMPRINT",EDGE,{"disambiguationData":[TD([[subQ2,-1.0]])],"derivedFrom":subQ1}),-1.0]])]});}
            var Q27;
            {var subQ5=sQuery(id+"F8.wireOp",EDGE,"E40.10.right");Q27=makeQuery(id+"F8.imprint","IMPRINT",FACE,{"disambiguationData":[TD([[makeQuery(id+"F8.imprint","IMPRINT",EDGE,{"derivedFrom":subQ5}),1.0]])]});}
            var Q28;
            {var subQ0=sQuery(id+"F8.wireOp",EDGE,"E34.filletArc");var subQ1=sQuery(id+"F8.wireOp",EDGE,"E31.left");var subQ2=makeQuery(id+"F8.imprint","INTERSECT",VERTEX,{"derivedFrom":[subQ1,subQ0]});Q28=makeQuery(id+"F8.imprint","IMPRINT",FACE,{"disambiguationData":[TD([[makeQuery(id+"F8.imprint","IMPRINT",EDGE,{"disambiguationData":[TD([[subQ2,1.0]])],"derivedFrom":subQ1}),-1.0]])]});}
            var Q29;
            {var subQ5=sQuery(id+"F8.wireOp",EDGE,"E40.9.right");Q29=makeQuery(id+"F8.imprint","IMPRINT",FACE,{"disambiguationData":[TD([[makeQuery(id+"F8.imprint","IMPRINT",EDGE,{"derivedFrom":subQ5}),1.0]])]});}
            var Q30;
            {var subQ0=sQuery(id+"F8.wireOp",EDGE,"E34.filletArc");var subQ1=sQuery(id+"F8.wireOp",EDGE,"E31.top");var subQ2=makeQuery(id+"F8.imprint","INTERSECT",VERTEX,{"derivedFrom":[subQ1,subQ0]});Q30=makeQuery(id+"F8.imprint","IMPRINT",FACE,{"disambiguationData":[TD([[makeQuery(id+"F8.imprint","IMPRINT",EDGE,{"disambiguationData":[TD([[subQ2,-1.0]])],"derivedFrom":subQ1}),-1.0]])]});}
            var Q31;
            {var subQ0=sQuery(id+"F8.wireOp",EDGE,"E34.filletArc");var subQ1=sQuery(id+"F8.wireOp",EDGE,"E31.top");var subQ2=makeQuery(id+"F8.imprint","INTERSECT",VERTEX,{"derivedFrom":[subQ1,subQ0]});Q31=makeQuery(id+"F8.imprint","IMPRINT",FACE,{"disambiguationData":[TD([[makeQuery(id+"F8.imprint","IMPRINT",EDGE,{"disambiguationData":[TD([[subQ2,-1.0]])],"derivedFrom":subQ1}),1.0]])]});}
            var Q32;
            {var subQ5=sQuery(id+"F8.wireOp",EDGE,"E40.8.right");Q32=makeQuery(id+"F8.imprint","IMPRINT",FACE,{"disambiguationData":[TD([[makeQuery(id+"F8.imprint","IMPRINT",EDGE,{"derivedFrom":subQ5}),1.0]])]});}
            var Q33;
            {var subQ0=sQuery(id+"F8.wireOp",EDGE,"E35.filletArc");var subQ1=sQuery(id+"F8.wireOp",EDGE,"E31.top");var subQ2=makeQuery(id+"F8.imprint","INTERSECT",VERTEX,{"derivedFrom":[subQ1,subQ0]});Q33=makeQuery(id+"F8.imprint","IMPRINT",FACE,{"disambiguationData":[TD([[makeQuery(id+"F8.imprint","IMPRINT",EDGE,{"disambiguationData":[TD([[subQ2,1.0]])],"derivedFrom":subQ1}),-1.0]])]});}
            var Q34;
            {var subQ5=sQuery(id+"F8.wireOp",EDGE,"E40.7.right");Q34=makeQuery(id+"F8.imprint","IMPRINT",FACE,{"disambiguationData":[TD([[makeQuery(id+"F8.imprint","IMPRINT",EDGE,{"derivedFrom":subQ5}),1.0]])]});}
            var Q35;
            {var subQ0=sQuery(id+"F8.wireOp",EDGE,"E35.filletArc");var subQ1=sQuery(id+"F8.wireOp",EDGE,"E31.right");var subQ2=makeQuery(id+"F8.imprint","INTERSECT",VERTEX,{"derivedFrom":[subQ1,subQ0]});Q35=makeQuery(id+"F8.imprint","IMPRINT",FACE,{"disambiguationData":[TD([[makeQuery(id+"F8.imprint","IMPRINT",EDGE,{"disambiguationData":[TD([[subQ2,1.0]])],"derivedFrom":subQ1}),1.0]])]});}
            var Q36;
            {var subQ5=sQuery(id+"F8.wireOp",EDGE,"E40.6.left");Q36=makeQuery(id+"F8.imprint","IMPRINT",FACE,{"disambiguationData":[TD([[makeQuery(id+"F8.imprint","IMPRINT",EDGE,{"derivedFrom":subQ5}),-1.0]])]});}
            var Q37;
            {var subQ0=sQuery(id+"F8.wireOp",EDGE,"E36.filletArc");var subQ1=sQuery(id+"F8.wireOp",EDGE,"E31.right");var subQ2=makeQuery(id+"F8.imprint","INTERSECT",VERTEX,{"derivedFrom":[subQ1,subQ0]});Q37=makeQuery(id+"F8.imprint","IMPRINT",FACE,{"disambiguationData":[TD([[makeQuery(id+"F8.imprint","IMPRINT",EDGE,{"disambiguationData":[TD([[subQ2,-1.0]])],"derivedFrom":subQ1}),1.0]])]});}
            var Q38;
            {var subQ5=sQuery(id+"F8.wireOp",EDGE,"E40.5.right");Q38=makeQuery(id+"F8.imprint","IMPRINT",FACE,{"disambiguationData":[TD([[makeQuery(id+"F8.imprint","IMPRINT",EDGE,{"derivedFrom":subQ5}),1.0]])]});}
            var Q39;
            {var subQ0=sQuery(id+"F8.wireOp",EDGE,"E36.filletArc");var subQ1=sQuery(id+"F8.wireOp",EDGE,"E33");var subQ2=makeQuery(id+"F8.imprint","INTERSECT",VERTEX,{"derivedFrom":[subQ1,subQ0]});Q39=makeQuery(id+"F8.imprint","IMPRINT",FACE,{"disambiguationData":[TD([[makeQuery(id+"F8.imprint","IMPRINT",EDGE,{"disambiguationData":[TD([[subQ2,1.0]])],"derivedFrom":subQ1}),1.0]])]});}
            var Q40;
            {var subQ5=sQuery(id+"F8.wireOp",EDGE,"E40.4.left");Q40=makeQuery(id+"F8.imprint","IMPRINT",FACE,{"disambiguationData":[TD([[makeQuery(id+"F8.imprint","IMPRINT",EDGE,{"derivedFrom":subQ5}),-1.0]])]});}
            var Q41;
            {var subQ0=sQuery(id+"F8.wireOp",EDGE,"E37.filletArc");var subQ1=sQuery(id+"F8.wireOp",EDGE,"E33");var subQ2=makeQuery(id+"F8.imprint","INTERSECT",VERTEX,{"derivedFrom":[subQ1,subQ0]});Q41=makeQuery(id+"F8.imprint","IMPRINT",FACE,{"disambiguationData":[TD([[makeQuery(id+"F8.imprint","IMPRINT",EDGE,{"disambiguationData":[TD([[subQ2,-1.0]])],"derivedFrom":subQ1}),1.0]])]});}
            var Q42;
            {var subQ5=sQuery(id+"F8.wireOp",EDGE,"E40.3.right");Q42=makeQuery(id+"F8.imprint","IMPRINT",FACE,{"disambiguationData":[TD([[makeQuery(id+"F8.imprint","IMPRINT",EDGE,{"derivedFrom":subQ5}),1.0]])]});}
            var Q43;
            {var subQ0=sQuery(id+"F8.wireOp",EDGE,"E37.filletArc");var subQ1=sQuery(id+"F8.wireOp",EDGE,"E31.bottom");var subQ2=makeQuery(id+"F8.imprint","INTERSECT",VERTEX,{"derivedFrom":[subQ1,subQ0]});Q43=makeQuery(id+"F8.imprint","IMPRINT",FACE,{"disambiguationData":[TD([[makeQuery(id+"F8.imprint","IMPRINT",EDGE,{"disambiguationData":[TD([[subQ2,1.0]])],"derivedFrom":subQ1}),1.0]])]});}
            var Q44;
            {var subQ5=sQuery(id+"F8.wireOp",EDGE,"E40.2.left");Q44=makeQuery(id+"F8.imprint","IMPRINT",FACE,{"disambiguationData":[TD([[makeQuery(id+"F8.imprint","IMPRINT",EDGE,{"derivedFrom":subQ5}),-1.0]])]});}
            var Q45;
            {var subQ0=sQuery(id+"F8.wireOp",EDGE,"E38.filletArc");var subQ1=sQuery(id+"F8.wireOp",EDGE,"E31.bottom");var subQ2=makeQuery(id+"F8.imprint","INTERSECT",VERTEX,{"derivedFrom":[subQ1,subQ0]});Q45=makeQuery(id+"F8.imprint","IMPRINT",FACE,{"disambiguationData":[TD([[makeQuery(id+"F8.imprint","IMPRINT",EDGE,{"disambiguationData":[TD([[subQ2,-1.0]])],"derivedFrom":subQ1}),1.0]])]});}
            var Q46;
            {var subQ5=sQuery(id+"F8.wireOp",EDGE,"E40.1.right");Q46=makeQuery(id+"F8.imprint","IMPRINT",FACE,{"disambiguationData":[TD([[makeQuery(id+"F8.imprint","IMPRINT",EDGE,{"derivedFrom":subQ5}),1.0]])]});}
            var Q47;
            {var subQ0=sQuery(id+"F8.wireOp",EDGE,"E38.filletArc");var subQ1=sQuery(id+"F8.wireOp",EDGE,"E32");var subQ2=makeQuery(id+"F8.imprint","INTERSECT",VERTEX,{"derivedFrom":[subQ1,subQ0]});Q47=makeQuery(id+"F8.imprint","IMPRINT",FACE,{"disambiguationData":[TD([[makeQuery(id+"F8.imprint","IMPRINT",EDGE,{"disambiguationData":[TD([[subQ2,1.0]])],"derivedFrom":subQ1}),1.0]])]});}
            extrude(context, id + "F9", {"entities" : qUnion([Q0, Q1, Q2, Q3, Q4, Q5, Q6, Q7, Q8, Q9, Q10, Q11, Q12, Q13, Q14, Q15, Q16, Q17, Q18, Q19, Q20, Q21, Q22, Q23, Q24, Q25, Q26, Q27, Q28, Q29, Q30, Q31, Q32, Q33, Q34, Q35, Q36, Q37, Q38, Q39, Q40, Q41, Q42, Q43, Q44, Q45, Q46, Q47]), "operationType" : NewBodyOperationType.ADD, "depth" : 11 * mm});
        }
        {
            var Q0;
            Q0=makeQuery(id+"F5.opExtrude","CAP_FACE",FACE,{"disambiguationData":[OSD([sQuery(id+"F4.wireOp",EDGE,"E14.bottom"),sQuery(id+"F4.wireOp",EDGE,"E14.top"),sQuery(id+"F4.wireOp",EDGE,"E16"),sQuery(id+"F4.wireOp",EDGE,"E17"),sQuery(id+"F4.wireOp",EDGE,"E18"),sQuery(id+"F4.wireOp",EDGE,"E19"),sQuery(id+"F4.wireOp",EDGE,"E20"),sQuery(id+"F4.wireOp",EDGE,"E21"),sQuery(id+"F4.wireOp",EDGE,"E22"),sQuery(id+"F4.wireOp",EDGE,"E23"),sQuery(id+"F4.wireOp",EDGE,"E24.filletArc"),sQuery(id+"F4.wireOp",EDGE,"E25.filletArc"),sQuery(id+"F4.wireOp",EDGE,"E26.filletArc"),sQuery(id+"F4.wireOp",EDGE,"E27.filletArc")])],"isStart":false});
            var sketch = newSketch(context, id + "F10", { "sketchPlane" : qUnion([Q0])});
            skCircle(sketch, "E41", {"center": v(-18, 2.36) * mm, "radius": 1.75 * mm});
            skCircle(sketch, "E42", {"center": v(18, 2.36) * mm, "radius": 1.75 * mm});
            skSolve(sketch);
        }
        {
            var Q0;
            Q0 = qSketchRegion(id + "F10", true);
            extrude(context, id + "F11", {"entities" : qUnion([Q0]), "oppositeDirection" : true, "depth" : 25 * mm});
        }
        {
            var Q0;
            {var subQ0=sQuery(id+"F6.wireOp",EDGE,"E30.bottom");var subQ1=sQuery(id+"F6.wireOp",EDGE,"E30.right");var subQ2=sQuery(id+"F6.wireOp",EDGE,"E30.left");var subQ3=sQuery(id+"F6.wireOp",EDGE,"E30.top");Q0=makeQuery(id+"F9.boolean.opBoolean","SPLIT",FACE,{"disambiguationData":[TD([makeQuery(id+"F7.opExtrude","SWEPT_FACE",FACE,{"disambiguationData":[OSD([subQ0])]})])],"derivedFrom":makeQuery(id+"F7.opExtrude","CAP_FACE",FACE,{"disambiguationData":[OSD([subQ0,subQ3,subQ2,subQ1])],"isStart":false})});}
            var sketch = newSketch(context, id + "F12", { "sketchPlane" : qUnion([Q0])});
            skCircle(sketch, "E43", {"center": v(-18, -2.36) * mm, "radius": 1.25 * mm});
            skCircle(sketch, "E44", {"center": v(18, -2.36) * mm, "radius": 1.4 * mm});
            skLineSegment(sketch, "E45", {"start": v(-27.59, -2.36) * mm, "end": v(31.45, -2.36) * mm, "construction": true});
            skArc(sketch, "E46", {"start": v(-20.68, -0.11) * mm, "mid": v(-21.5, -2.36) * mm, "end": v(-20.68, -4.6) * mm});
            skArc(sketch, "E47", {"start": v(20.68, -4.6) * mm, "mid": v(21.5, -2.36) * mm, "end": v(20.68, -0.11) * mm});
            skLineSegment(sketch, "E48", {"start": v(-16.1, 5.36) * mm, "end": v(-20.68, -0.11) * mm});
            skLineSegment(sketch, "E49", {"start": v(-22.57, -2.36) * mm, "end": v(-22.43, -2.53) * mm});
            skLineSegment(sketch, "E50", {"start": v(16.1, 5.36) * mm, "end": v(20.68, -0.11) * mm});
            skLineSegment(sketch, "E51", {"start": v(20.68, -4.6) * mm, "end": v(16.1, -10.08) * mm});
            skLineSegment(sketch, "E52.trimOffspring", {"start": v(-20.68, -4.6) * mm, "end": v(-16.1, -10.08) * mm});
            skLineSegment(sketch, "E53", {"start": v(-16.1, 5.36) * mm, "end": v(-16.1, -10.08) * mm});
            skLineSegment(sketch, "E54", {"start": v(16.1, 5.36) * mm, "end": v(16.1, -10.08) * mm});
            skSolve(sketch);
        }
        {
            var Q0;
            Q0=makeQuery(id+"F12.imprint","IMPRINT",FACE,{"disambiguationData":[TD([[makeQuery(id+"F12.imprint","IMPRINT",EDGE,{"derivedFrom":sQuery(id+"F12.wireOp",EDGE,"E43")}),-1.0]])]});
            var Q1;
            Q1=makeQuery(id+"F12.imprint","IMPRINT",FACE,{"disambiguationData":[TD([[makeQuery(id+"F12.imprint","IMPRINT",EDGE,{"derivedFrom":sQuery(id+"F12.wireOp",EDGE,"E44")}),-1.0]])]});
            extrude(context, id + "F13", {"entities" : qUnion([Q0, Q1]), "operationType" : NewBodyOperationType.ADD, "depth" : 5 * mm});
        }
        {
            var Q0;
            Q0=makeQuery(id+"F9.opExtrude","CAP_FACE",FACE,{"disambiguationData":[OSD([sQuery(id+"F8.wireOp",EDGE,"E40.0.left"),sQuery(id+"F8.wireOp",EDGE,"E40.0.right"),sQuery(id+"F8.wireOp",EDGE,"E40.1.left"),sQuery(id+"F8.wireOp",EDGE,"E40.1.right"),sQuery(id+"F8.wireOp",EDGE,"E40.2.left"),sQuery(id+"F8.wireOp",EDGE,"E40.2.right"),sQuery(id+"F8.wireOp",EDGE,"E40.3.left"),sQuery(id+"F8.wireOp",EDGE,"E40.3.right"),sQuery(id+"F8.wireOp",EDGE,"E40.4.left"),sQuery(id+"F8.wireOp",EDGE,"E40.4.right"),sQuery(id+"F8.wireOp",EDGE,"E40.5.left"),sQuery(id+"F8.wireOp",EDGE,"E40.5.right"),sQuery(id+"F8.wireOp",EDGE,"E40.6.left"),sQuery(id+"F8.wireOp",EDGE,"E40.6.right"),sQuery(id+"F8.wireOp",EDGE,"E40.7.left"),sQuery(id+"F8.wireOp",EDGE,"E40.7.right"),sQuery(id+"F8.wireOp",EDGE,"E40.8.left"),sQuery(id+"F8.wireOp",EDGE,"E40.8.right"),sQuery(id+"F8.wireOp",EDGE,"E40.9.left"),sQuery(id+"F8.wireOp",EDGE,"E40.9.right"),sQuery(id+"F8.wireOp",EDGE,"E40.10.left"),sQuery(id+"F8.wireOp",EDGE,"E40.10.right"),sQuery(id+"F8.wireOp",EDGE,"E40.11.left"),sQuery(id+"F8.wireOp",EDGE,"E40.11.right")])],"isStart":false});
            var sketch = newSketch(context, id + "F14", { "sketchPlane" : qUnion([Q0])});
            skLineSegment(sketch, "E55.bottom", {"start": v(-6.2, 15.99) * mm, "end": v(6.2, 15.99) * mm});
            skLineSegment(sketch, "E55.top", {"start": v(-12.35, -20.71) * mm, "end": v(12.35, -20.71) * mm});
            skLineSegment(sketch, "E55.left", {"start": v(-16.1, 5.36) * mm, "end": v(-16.1, -16.96) * mm});
            skLineSegment(sketch, "E55.right", {"start": v(16.1, 5.36) * mm, "end": v(16.1, -16.96) * mm});
            skLineSegment(sketch, "E56", {"start": v(-15.15, 7.86) * mm, "end": v(-9, 14.74) * mm});
            skLineSegment(sketch, "E57", {"start": v(9, 14.74) * mm, "end": v(15.15, 7.86) * mm});
            skPoint(sketch, "E58.visualSharp", {"position": v(-16.1, 6.79) * mm});
            skArc(sketch, "E58.filletArc", {"start": v(-15.15, 7.86) * mm, "mid": v(-15.85, 6.7) * mm, "end": v(-16.1, 5.36) * mm});
            skPoint(sketch, "E59.visualSharp", {"position": v(-16.1, -20.71) * mm});
            skArc(sketch, "E59.filletArc", {"start": v(-16.1, -16.96) * mm, "mid": v(-15, -19.61) * mm, "end": v(-12.35, -20.71) * mm});
            skPoint(sketch, "E60.visualSharp", {"position": v(16.1, -20.71) * mm});
            skArc(sketch, "E60.filletArc", {"start": v(12.35, -20.71) * mm, "mid": v(15, -19.61) * mm, "end": v(16.1, -16.96) * mm});
            skPoint(sketch, "E61.visualSharp", {"position": v(-7.88, 15.99) * mm});
            skArc(sketch, "E61.filletArc", {"start": v(-6.2, 15.99) * mm, "mid": v(-7.73, 15.66) * mm, "end": v(-9, 14.74) * mm});
            skPoint(sketch, "E62.visualSharp", {"position": v(7.88, 15.99) * mm});
            skArc(sketch, "E62.filletArc", {"start": v(9, 14.74) * mm, "mid": v(7.73, 15.66) * mm, "end": v(6.2, 15.99) * mm});
            skPoint(sketch, "E63.visualSharp", {"position": v(16.1, 6.79) * mm});
            skArc(sketch, "E63.filletArc", {"start": v(16.1, 5.36) * mm, "mid": v(15.85, 6.7) * mm, "end": v(15.15, 7.86) * mm});
            skLineSegment(sketch, "E64.bottom", {"start": v(-3.58, 8.64) * mm, "end": v(3.58, 8.64) * mm});
            skLineSegment(sketch, "E64.top", {"start": v(-3.58, 6.84) * mm, "end": v(3.58, 6.84) * mm});
            skLineSegment(sketch, "E64.left", {"start": v(-3.58, 8.64) * mm, "end": v(-3.58, 6.84) * mm});
            skLineSegment(sketch, "E64.right", {"start": v(3.58, 8.64) * mm, "end": v(3.58, 6.84) * mm});
            skLineSegment(sketch, "E65.bottom", {"start": v(-10.65, -0.56) * mm, "end": v(-3.5, -0.56) * mm});
            skLineSegment(sketch, "E65.top", {"start": v(-10.65, -2.36) * mm, "end": v(-3.5, -2.36) * mm});
            skLineSegment(sketch, "E65.left", {"start": v(-10.65, -0.56) * mm, "end": v(-10.65, -2.36) * mm});
            skLineSegment(sketch, "E65.right", {"start": v(-3.5, -0.56) * mm, "end": v(-3.5, -2.36) * mm});
            skLineSegment(sketch, "E66.bottom", {"start": v(-11.45, -13.56) * mm, "end": v(-4.3, -13.56) * mm});
            skLineSegment(sketch, "E66.top", {"start": v(-11.45, -15.36) * mm, "end": v(-4.3, -15.36) * mm});
            skLineSegment(sketch, "E66.left", {"start": v(-11.45, -13.56) * mm, "end": v(-11.45, -15.36) * mm});
            skLineSegment(sketch, "E66.right", {"start": v(-4.3, -13.56) * mm, "end": v(-4.3, -15.36) * mm});
            skSolve(sketch);
        }
        {
            var Q0;
            Q0 = qSketchRegion(id + "F14", true);
            extrude(context, id + "F15", {"entities" : qUnion([Q0]), "operationType" : NewBodyOperationType.ADD, "depth" : 1.5 * mm});
        }
        {
            var Q0;
            Q0=makeQuery(id+"F15.opExtrude","CAP_EDGE",EDGE,{"disambiguationData":[OSD([sQuery(id+"F14.wireOp",EDGE,"E55.top")])],"isStart":false});
            var Q1;
            Q1=makeQuery(id+"F13.opExtrude","CAP_EDGE",EDGE,{"disambiguationData":[OSD([sQuery(id+"F12.wireOp",EDGE,"E52.trimOffspring")])],"isStart":false});
            var Q2;
            Q2=makeQuery(id+"F13.opExtrude","CAP_EDGE",EDGE,{"disambiguationData":[OSD([sQuery(id+"F12.wireOp",EDGE,"E51")])],"isStart":false});
            fillet(context, id + "F16", {"entities" : qUnion([Q0, Q1, Q2]), "radius" : 1 * mm, "tangentPropagation" : true, "allowEdgeOverflow" : false});
        }
    });
